# Revit family: Heat Pump-Rheem-W2W-35kW A
name_source: partatom
category: Mechanical Equipment
revit_build: Autodesk Revit 2016 (Build: 20190508_0715(x64)
units: mm (PartAtom-declared; Revit-internal decimal feet)

## family parameters
Always vertical = Yes
Cut with Voids When Loaded = No
OmniClass Number = 23.75.10.21
OmniClass Title = Heat Pumps
Part Type = Normal
Room Calculation Point = No
Round Connector Dimension = Use Radius
Shared = No
Work Plane-Based = No

## types (2) — shared parameters
ApparentLoad_ANZRS = 35 kW
InletPipeDiameter = 50 mm  [stored 0.164042 ft]
Length_ANZRS = 1049 mm  [stored 3.4416 ft]
Manufacturer = Rheem
Material_ANZRS = Rheem-Steel-Grey
OutletPipeDiameter = 50 mm  [stored 0.164042 ft]
PowerFactor_ANZRS = 1
SupportInsetSide = 77 mm  [stored 0.252625 ft]
URL = https://www.rheem.com.au
Voltage_ANZRS = 230 V
Wattage_ANZRS = 35 kW
Width_ANZRS = 599 mm  [stored 1.96522 ft]
calcFanGuardDepth = 133 mm  [stored 0.436352 ft]
calcInletPipeRadius = 25 mm  [stored 0.082021 ft]
calcOutletPipeRad = 25 mm  [stored 0.082021 ft]

## per-type parameters (varying)
| type | Description | Height_ANZRS | Model | Show Top Supports | calcTopSupport |
| 95403500 | Rheem's Commercial Water to Water (W2W) heat pump includes units using R134a for hot water heating up to 65°C, with a minimum entering water temperature on the building loop of 12°C, giving a return water temperature of 7°C, with the units being compact and suitable for indoor or external installation. | 827 mm  [stored 2.71325 ft] | Rheem Commercial Water to Water Heat Pump – 35kW | No | 0 mm  [stored 0 ft] |
| 9540350S | Rheem's Commercial Water to Water (W2W) heat pump includes units using R134a for hot water heating up to 65°C, with a minimum entering water temperature on the building loop of 12°C, giving a return water temperature of 7°C, with the units being compact and suitable for indoor or external installation. Stackable models allow units to be stacked two high for reduced footprint. | 859 mm  [stored 2.81824 ft] | Rheem Commercial Water to Water Heat Pump – 35kW Stackable Model | Yes | 32 mm  [stored 0.104987 ft] |

note: column(s) folded — value = type name in every type: ProductCode_ANZRS

note: [stored X ft] marks values corroborated as IEEE doubles in the binary element streams (Revit-internal decimal feet)

## geometry (parser evidence)
native form markers: Blend x8, Sweep x11
no freeform markers — native parametric forms only
